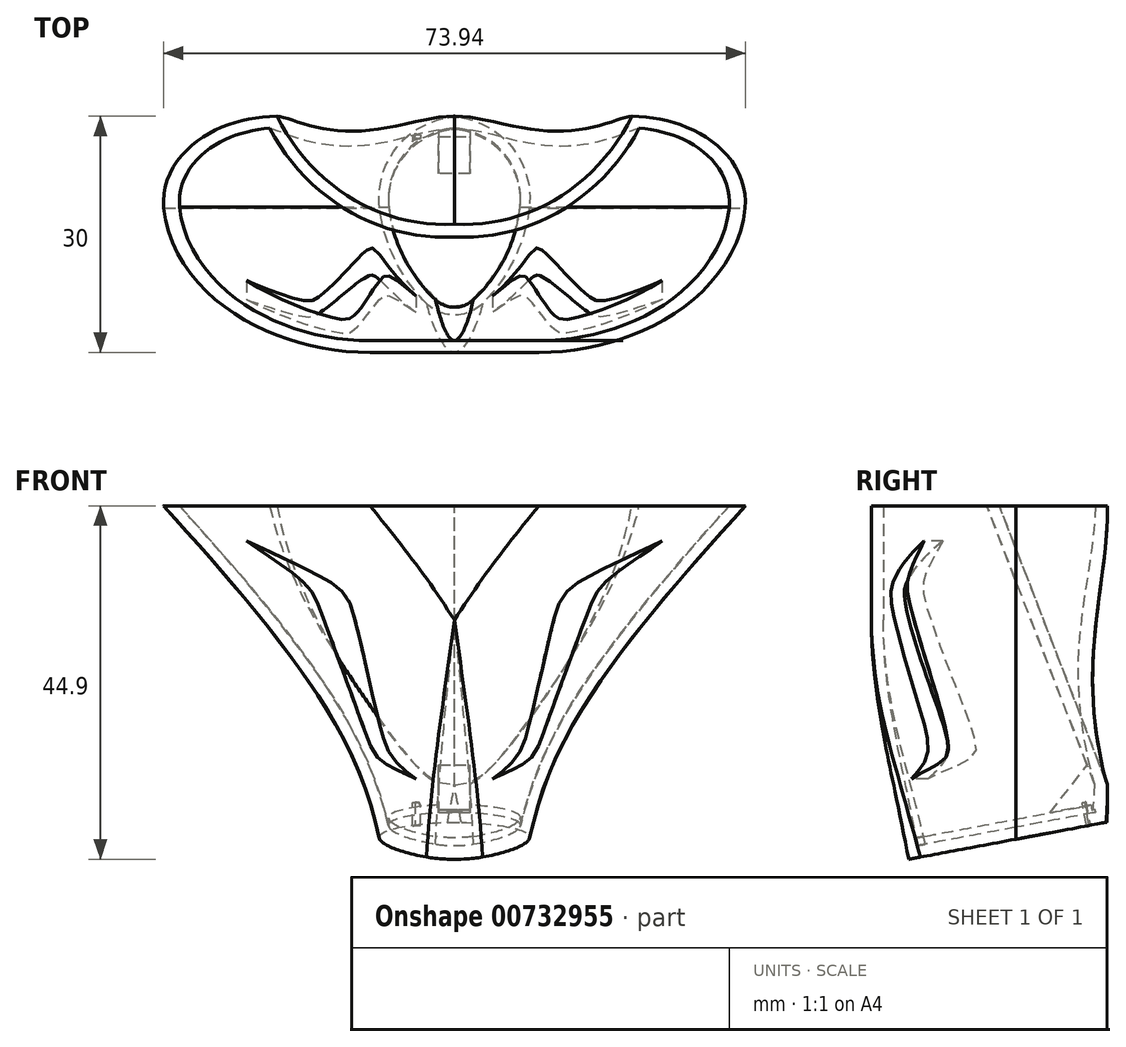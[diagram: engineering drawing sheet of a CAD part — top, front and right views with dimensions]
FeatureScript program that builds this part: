
annotation { "Feature Type Name" : "Feature", "Feature Type Description" : "" }
export const myFeature = defineFeature(function(context is Context, id is Id, definition is map)
    precondition{}
    {
        {
            var Q0;
            Q0=qCreatedBy(makeId("Front.planeOp"),FACE);
            var sketch = newSketch(context, id + "F0", { "sketchPlane" : qUnion([Q0])});
            skLineSegment(sketch, "E0", {"start": v(-9, -21.86) * mm, "end": v(9, -21.86) * mm});
            skLineSegment(sketch, "E1", {"start": v(0, -21.86) * mm, "end": v(0, 23.14) * mm, "construction": true});
            skLineSegment(sketch, "E2", {"start": v(-37, 23.14) * mm, "end": v(37, 23.14) * mm});
            skFitSpline(sketch, "E3", {"points": [v(-37, 23.14) * mm, v(-9, -21.86) * mm], "startDerivative": vector(66.87, -73.39) * mm, "endDerivative": vector(7.33, -37.29) * mm});
            skFitSpline(sketch, "E4.MirrorCS", {"points": [v(37, 23.14) * mm, v(9, -21.86) * mm], "startDerivative": vector(-66.87, -73.39) * mm, "endDerivative": vector(-7.33, -37.29) * mm});
            skSolve(sketch);
        }
        {
            var Q0;
            Q0=makeQuery(id+"F0.imprint","IMPRINT",FACE,{"disambiguationData":[TD([[makeQuery(id+"F0.imprint","IMPRINT",EDGE,{"derivedFrom":sQuery(id+"F0.wireOp",EDGE,"E0")}),1.0]])]});
            extrude(context, id + "F1", {"entities" : qUnion([Q0]), "depth" : 30 * mm, "offsetDistance" : 25 * mm});
        }
        {
            var Q0;
            Q0=makeQuery(id+"F1.opExtrude","CAP_EDGE",EDGE,{"disambiguationData":[OSD([sQuery(id+"F0.wireOp",EDGE,"E3")])],"isStart":false});
            var Q1;
            Q1=makeQuery(id+"F1.opExtrude","CAP_EDGE",EDGE,{"disambiguationData":[OSD([sQuery(id+"F0.wireOp",EDGE,"E4.MirrorCS")])],"isStart":false});
            fillet(context, id + "F2", {"entities" : qUnion([Q0, Q1]), "radius" : 19.8 * mm, "tangentPropagation" : true, "allowEdgeOverflow" : false});
        }
        {
            var Q0;
            Q0=makeQuery(id+"F1.opExtrude","CAP_EDGE",EDGE,{"disambiguationData":[OSD([sQuery(id+"F0.wireOp",EDGE,"E3")])],"isStart":true});
            var Q1;
            Q1=makeQuery(id+"F1.opExtrude","CAP_EDGE",EDGE,{"disambiguationData":[OSD([sQuery(id+"F0.wireOp",EDGE,"E4.MirrorCS")])],"isStart":true});
            fillet(context, id + "F3", {"entities" : qUnion([Q0, Q1]), "radius" : 10.86 * mm, "tangentPropagation" : true, "allowEdgeOverflow" : false});
        }
        {
            var Q0;
            Q0=makeQuery(id+"F2.opFillet","BLEND_EDGE",EDGE,{"blendedFrom":[makeQuery(id+"F1.opExtrude","CAP_EDGE",EDGE,{"disambiguationData":[OSD([sQuery(id+"F0.wireOp",EDGE,"E3")])],"isStart":false}),makeQuery(id+"F1.opExtrude","CAP_EDGE",EDGE,{"disambiguationData":[OSD([sQuery(id+"F0.wireOp",EDGE,"E4.MirrorCS")])],"isStart":false})],"blendedInto":[]});
            fillet(context, id + "F4", {"entities" : qUnion([Q0]), "radius" : 5 * mm, "tangentPropagation" : true, "allowEdgeOverflow" : false});
        }
        {
            var Q0;
            Q0=makeQuery(id+"F3.opFillet","BLEND_EDGE",EDGE,{"blendedFrom":[makeQuery(id+"F1.opExtrude","CAP_EDGE",EDGE,{"disambiguationData":[OSD([sQuery(id+"F0.wireOp",EDGE,"E3")])],"isStart":true}),makeQuery(id+"F1.opExtrude","CAP_EDGE",EDGE,{"disambiguationData":[OSD([sQuery(id+"F0.wireOp",EDGE,"E4.MirrorCS")])],"isStart":true})],"blendedInto":[]});
            fillet(context, id + "F5", {"entities" : qUnion([Q0]), "radius" : 5 * mm, "tangentPropagation" : true, "allowEdgeOverflow" : false});
        }
        {
            var Q0;
            Q0=qCreatedBy(makeId("Right.planeOp"),FACE);
            var sketch = newSketch(context, id + "F6", { "sketchPlane" : qUnion([Q0])});
            skLineSegment(sketch, "E5", {"start": v(-31.86, -23) * mm, "end": v(8.16, -15.5) * mm});
            skLineSegment(sketch, "E6", {"start": v(8.16, -15.5) * mm, "end": v(3.01, -25.08) * mm});
            skLineSegment(sketch, "E7", {"start": v(3.01, -25.08) * mm, "end": v(-31.86, -23) * mm});
            skSolve(sketch);
        }
        {
            var Q0;
            Q0=qSketchRegion(id+"F6",true);
            extrude(context, id + "F7", {"entities" : qUnion([Q0]), "operationType" : NewBodyOperationType.REMOVE, "depth" : 25 * mm, "offsetDistance" : 25 * mm, "hasSecondDirection" : true, "secondDirectionOppositeDirection" : true, "secondDirectionDepth" : 25 * mm});
        }
        {
            var Q0;
            Q0=qCreatedBy(makeId("Right.planeOp"),FACE);
            var sketch = newSketch(context, id + "F8", { "sketchPlane" : qUnion([Q0])});
            skLineSegment(sketch, "E8", {"start": v(-18.8, 36.28) * mm, "end": v(0, 43.57) * mm});
            skSolve(sketch);
        }
        {
            var Q0;
            Q0=sQuery(id+"F8.wireOp",EDGE,"E8");
            extrude(context, id + "F9", {"bodyType" : ToolBodyType.SURFACE, "surfaceEntities" : qUnion([Q0]), "depth" : 25 * mm, "offsetDistance" : 25 * mm, "hasSecondDirection" : true, "secondDirectionOppositeDirection" : true, "secondDirectionDepth" : 25 * mm});
        }
        {
            var Q0;
            Q0=makeQuery(id+"F9.opExtrude","SWEPT_FACE",FACE,{"disambiguationData":[OSD([sQuery(id+"F8.wireOp",EDGE,"E8")])]});
            var sketch = newSketch(context, id + "F10", { "sketchPlane" : qUnion([Q0])});
            skArc(sketch, "E9", {"start": v(23.67, -10.78) * mm, "mid": v(14.28, 0.64) * mm, "end": v(0, 4.43) * mm});
            skFitSpline(sketch, "E10", {"points": [v(23.67, -10.78) * mm, v(31.63, -8.58) * mm], "startDerivative": vector(3.77, -5) * mm, "endDerivative": vector(13, 4.88) * mm});
            skLineSegment(sketch, "E11", {"start": v(31.63, -8.58) * mm, "end": v(10.84, -28.18) * mm});
            skLineSegment(sketch, "E12", {"start": v(10.84, -28.18) * mm, "end": v(0, -18.9) * mm});
            skLineSegment(sketch, "E13", {"start": v(0, 4.27) * mm, "end": v(0, -45.58) * mm, "construction": true});
            skFitSpline(sketch, "E14.MirrorCS", {"points": [v(-23.67, -10.78) * mm, v(-31.63, -8.58) * mm], "startDerivative": vector(-3.77, -5) * mm, "endDerivative": vector(-13, 4.88) * mm});
            skLineSegment(sketch, "E15.MirrorCS", {"start": v(-31.63, -8.58) * mm, "end": v(-10.84, -28.18) * mm});
            skLineSegment(sketch, "E16.MirrorCS", {"start": v(-10.84, -28.18) * mm, "end": v(0, -18.9) * mm});
            skArc(sketch, "E17.MirrorCS", {"start": v(-23.67, -10.78) * mm, "mid": v(-14.28, 0.64) * mm, "end": v(0, 4.43) * mm});
            skPoint(sketch, "E18.orphan", {"position": v(-24.25, -12.44) * mm});
            skPoint(sketch, "E19.orphan", {"position": v(24.25, -12.44) * mm});
            skSolve(sketch);
        }
        {
            var Q0;
            Q0=qSketchRegion(id+"F10",true);
            extrude(context, id + "F11", {"entities" : qUnion([Q0]), "operationType" : NewBodyOperationType.REMOVE, "depth" : 77.2 * mm, "offsetDistance" : 25 * mm});
        }
        {
            var Q0;
            Q0=makeQuery(id+"F9.opExtrude","SWEPT_BODY",BODY,{"disambiguationData":[OSD([sQuery(id+"F8.wireOp",EDGE,"E8")])]});
            deleteBodies(context, id + "F12", {"entities" : qUnion([Q0])});
        }
        {
            var Q0;
            Q0=makeQuery(id+"F1.opExtrude","SWEPT_FACE",FACE,{"disambiguationData":[OSD([sQuery(id+"F0.wireOp",EDGE,"E2")])]});
            shell(context, id + "F13", {"entities" : qUnion([Q0]), "thickness" : 1.5 * mm});
        }
        {
            var Q0;
            Q0=makeQuery(id+"F7.boolean.opBoolean","COPY",FACE,{"derivedFrom":makeQuery(id+"F7.opExtrude","SWEPT_FACE",FACE,{"disambiguationData":[OSD([sQuery(id+"F6.wireOp",EDGE,"E5")])]})});
            var sketch = newSketch(context, id + "F14", { "sketchPlane" : qUnion([Q0])});
            skFitSpline(sketch, "E20", {"points": [v(-5.51, 5.37) * mm, v(-2.87, 6.42) * mm, v(-2.97, 9.84) * mm, v(-3.98, 12.81) * mm, v(-3.33, 18.18) * mm, v(0, 21.05) * mm], "startDerivative": vector(11.33, -0.98) * mm, "endDerivative": vector(19.02, -2.14) * mm});
            skFitSpline(sketch, "E21.MirrorCS", {"points": [v(5.51, 5.37) * mm, v(2.87, 6.42) * mm, v(2.97, 9.84) * mm, v(3.98, 12.81) * mm, v(3.33, 18.18) * mm, v(0, 21.05) * mm], "startDerivative": vector(-11.33, -0.98) * mm, "endDerivative": vector(-19.02, -2.14) * mm});
            skFitSpline(sketch, "E22", {"points": [v(0, 27.88) * mm, v(-2.51, 27.15) * mm, v(-6.1, 22.7) * mm, v(-7.89, 18.78) * mm, v(-8.68, 15.18) * mm, v(-8.46, 11.07) * mm, v(-6.69, 7.46) * mm, v(-4.98, 5.4) * mm], "startDerivative": vector(-23.61, -0.54) * mm, "endDerivative": vector(20.39, -26.15) * mm});
            skArc(sketch, "E23.filletArc", {"start": v(-5.35, 5.86) * mm, "mid": v(-4.87, 5.54) * mm, "end": v(-4.3, 5.54) * mm});
            skFitSpline(sketch, "E24.MirrorCS", {"points": [v(0, 27.88) * mm, v(2.51, 27.15) * mm, v(6.1, 22.7) * mm, v(7.89, 18.78) * mm, v(8.68, 15.18) * mm, v(8.46, 11.07) * mm, v(6.69, 7.46) * mm, v(4.98, 5.4) * mm], "startDerivative": vector(23.61, -0.54) * mm, "endDerivative": vector(-20.39, -26.15) * mm});
            skArc(sketch, "E25.MirrorCS", {"start": v(5.35, 5.86) * mm, "mid": v(4.87, 5.54) * mm, "end": v(4.3, 5.54) * mm});
            skSolve(sketch);
        }
        {
            var Q0;
            Q0=makeQuery(id+"F14.imprint","IMPRINT",FACE,{"disambiguationData":[TD([[makeQuery(id+"F14.imprint","IMPRINT",EDGE,{"derivedFrom":sQuery(id+"F14.wireOp",EDGE,"E20")}),1.0]])]});
            extrude(context, id + "F15", {"entities" : qUnion([Q0]), "operationType" : NewBodyOperationType.REMOVE, "oppositeDirection" : true, "depth" : 3 * mm, "offsetDistance" : 25 * mm});
        }
        {
            var Q0;
            Q0=qCreatedBy(makeId("Right.planeOp"),FACE);
            var sketch = newSketch(context, id + "F16", { "sketchPlane" : qUnion([Q0])});
            skLineSegment(sketch, "E26", {"start": v(-7.62, -16.24) * mm, "end": v(-2.06, -9.1) * mm});
            skLineSegment(sketch, "E27", {"start": v(-2.06, -9.1) * mm, "end": v(-0.48, -15.33) * mm});
            skLineSegment(sketch, "E28", {"start": v(-0.48, -15.33) * mm, "end": v(-7.62, -16.24) * mm});
            skSolve(sketch);
        }
        {
            var Q0;
            Q0=qSketchRegion(id+"F16",true);
            extrude(context, id + "F17", {"entities" : qUnion([Q0]), "operationType" : NewBodyOperationType.ADD, "depth" : 2 * mm, "offsetDistance" : 25 * mm, "hasSecondDirection" : true, "secondDirectionOppositeDirection" : true, "secondDirectionDepth" : 2 * mm});
        }
        {
            var Q0;
            Q0=makeQuery(id+"F14.imprint","IMPRINT",FACE,{"disambiguationData":[TD([[makeQuery(id+"F14.imprint","IMPRINT",EDGE,{"derivedFrom":sQuery(id+"F14.wireOp",EDGE,"E20")}),1.0]])]});
            extrude(context, id + "F18", {"entities" : qUnion([Q0]), "operationType" : NewBodyOperationType.REMOVE, "oppositeDirection" : true, "depth" : 3 * mm, "offsetDistance" : 25 * mm});
        }
        {
            var Q0;
            Q0=makeQuery(id+"F15.boolean.opBoolean","SPLIT",FACE,{"disambiguationData":[TD([makeQuery(id+"F13.opShell","OFFSET_FACE",FACE,{"disambiguationData":[OSD([sQuery(id+"F10.wireOp",EDGE,"E9")])]})])],"derivedFrom":makeQuery(id+"F13.opShell","OFFSET_FACE",FACE,{"disambiguationData":[OSD([sQuery(id+"F6.wireOp",EDGE,"E5")])]})});
            extrude(context, id + "F19", {"entities" : qUnion([Q0]), "operationType" : NewBodyOperationType.ADD, "depth" : 1 * mm, "offsetDistance" : 25 * mm});
        }
        {
            var Q0;
            Q0=makeQuery(id+"F1.opExtrude","CAP_FACE",FACE,{"disambiguationData":[OSD([sQuery(id+"F0.wireOp",EDGE,"E0"),sQuery(id+"F0.wireOp",EDGE,"E2"),sQuery(id+"F0.wireOp",EDGE,"E3"),sQuery(id+"F0.wireOp",EDGE,"E4.MirrorCS")])],"isStart":false});
            var sketch = newSketch(context, id + "F20", { "sketchPlane" : qUnion([Q0])});
            skFitSpline(sketch, "E29", {"points": [v(26.39, 18.67) * mm, v(17.16, 10.14) * mm, v(10.98, -6.5) * mm, v(4.85, -11.53) * mm], "startDerivative": vector(-69, -47.58) * mm, "endDerivative": vector(-56.44, -25.14) * mm});
            skFitSpline(sketch, "E30", {"points": [v(26.39, 18.67) * mm, v(12.8, 9.26) * mm, v(9.3, -5.4) * mm, v(4.85, -11.53) * mm], "startDerivative": vector(-93.73, -44.21) * mm, "endDerivative": vector(-36.1, -25.12) * mm});
            skFitSpline(sketch, "E31.MirrorCS", {"points": [v(-26.39, 18.67) * mm, v(-12.8, 9.26) * mm, v(-9.3, -5.4) * mm, v(-4.85, -11.53) * mm], "startDerivative": vector(93.73, -44.21) * mm, "endDerivative": vector(36.1, -25.12) * mm});
            skFitSpline(sketch, "E32.MirrorCS", {"points": [v(-26.39, 18.67) * mm, v(-17.16, 10.14) * mm, v(-10.98, -6.5) * mm, v(-4.85, -11.53) * mm], "startDerivative": vector(69, -47.58) * mm, "endDerivative": vector(56.44, -25.14) * mm});
            skSolve(sketch);
        }
        {
            var Q0;
            Q0=makeQuery(id+"F20.imprint","IMPRINT",FACE,{"disambiguationData":[TD([[makeQuery(id+"F20.imprint","IMPRINT",EDGE,{"derivedFrom":sQuery(id+"F20.wireOp",EDGE,"E31.MirrorCS")}),-1.0]])]});
            var Q1;
            Q1=makeQuery(id+"F20.imprint","IMPRINT",FACE,{"disambiguationData":[TD([[makeQuery(id+"F20.imprint","IMPRINT",EDGE,{"derivedFrom":sQuery(id+"F20.wireOp",EDGE,"E29")}),-1.0]])]});
            extrude(context, id + "F21", {"entities" : qUnion([Q0, Q1]), "operationType" : NewBodyOperationType.REMOVE, "oppositeDirection" : true, "depth" : 15 * mm, "offsetDistance" : 25 * mm});
        }
    });
